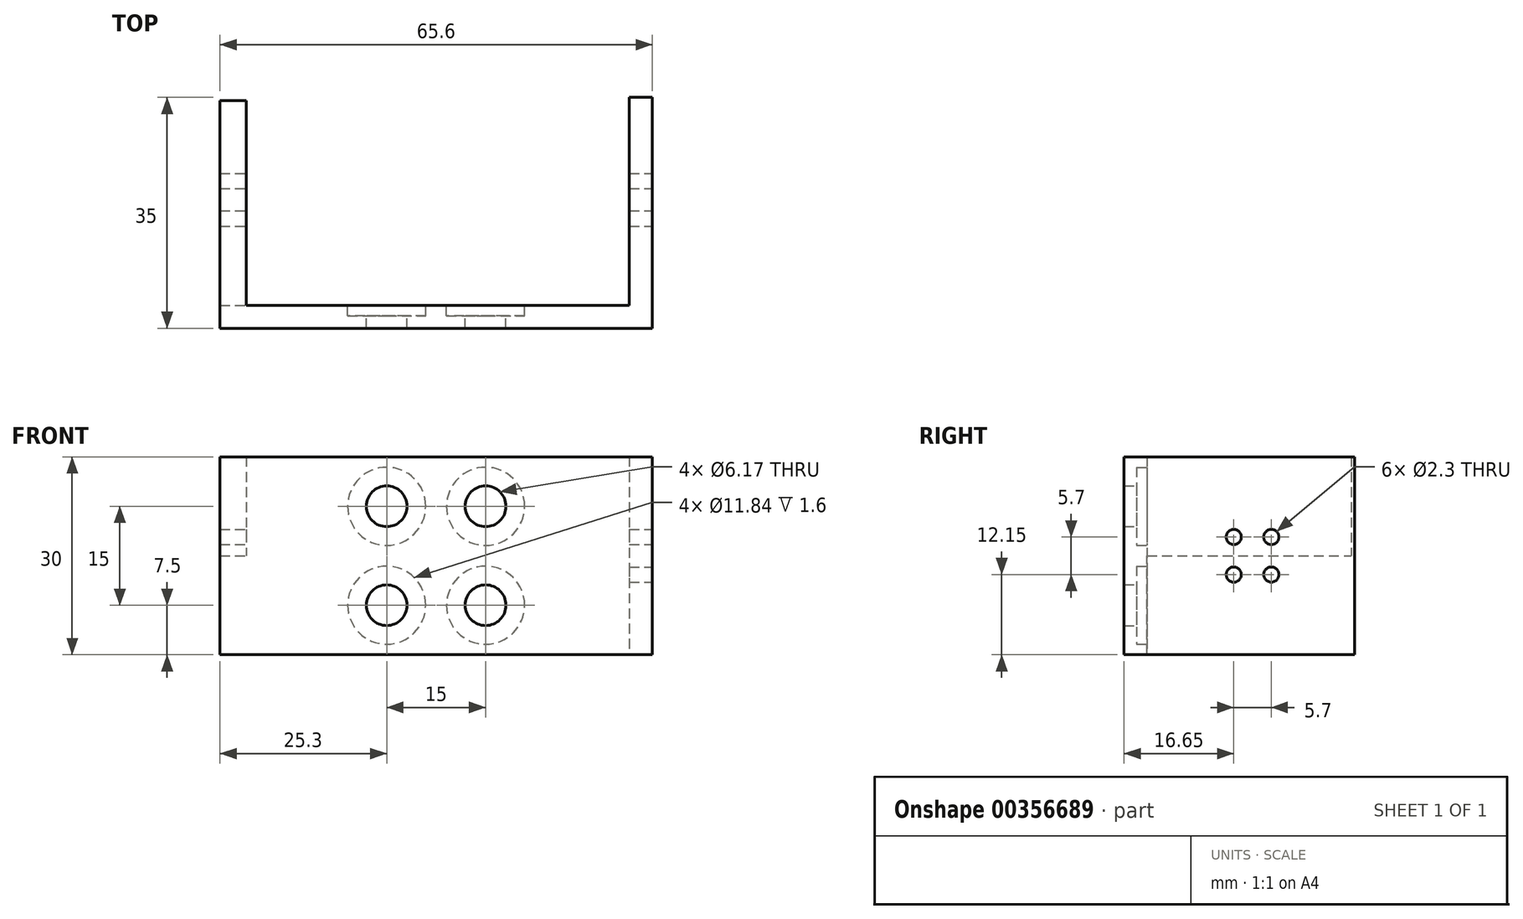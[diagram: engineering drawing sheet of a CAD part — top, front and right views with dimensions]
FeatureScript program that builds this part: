
annotation { "Feature Type Name" : "Feature", "Feature Type Description" : "" }
export const myFeature = defineFeature(function(context is Context, id is Id, definition is map)
    precondition{}
    {
        {
            var Q0;
            Q0=qCreatedBy(makeId("Front.planeOp"),FACE);
            var sketch = newSketch(context, id + "F0", { "sketchPlane" : qUnion([Q0])});
            skLineSegment(sketch, "E0.bottom", {"start": v(32.8, -15) * mm, "end": v(-32.8, -15) * mm});
            skLineSegment(sketch, "E0.top", {"start": v(32.8, 15) * mm, "end": v(-32.8, 15) * mm});
            skLineSegment(sketch, "E0.left", {"start": v(32.8, -15) * mm, "end": v(32.8, 15) * mm});
            skLineSegment(sketch, "E0.right", {"start": v(-32.8, -15) * mm, "end": v(-32.8, 15) * mm});
            skPoint(sketch, "E0.middle", {"position": v(0, 0) * mm});
            skSolve(sketch);
        }
        {
            var Q0;
            Q0=qSketchRegion(id+"F0",true);
            extrude(context, id + "F1", {"entities" : qUnion([Q0]), "endBound" : BoundingType.SYMMETRIC, "depth" : 3.5 * mm});
        }
        {
            var Q0;
            Q0=qCreatedBy(makeId("Top.planeOp"),FACE);
            var sketch = newSketch(context, id + "F2", { "sketchPlane" : qUnion([Q0])});
            skLineSegment(sketch, "E1.bottom", {"start": v(32.8, 1.75) * mm, "end": v(29.3, 1.75) * mm});
            skLineSegment(sketch, "E1.top", {"start": v(32.8, 33.25) * mm, "end": v(29.3, 33.25) * mm});
            skLineSegment(sketch, "E1.left", {"start": v(32.8, 1.75) * mm, "end": v(32.8, 33.25) * mm});
            skLineSegment(sketch, "E1.right", {"start": v(29.3, 1.75) * mm, "end": v(29.3, 33.25) * mm});
            skSolve(sketch);
        }
        {
            var Q0;
            Q0=qSketchRegion(id+"F2",true);
            extrude(context, id + "F3", {"entities" : qUnion([Q0]), "operationType" : NewBodyOperationType.ADD, "endBound" : BoundingType.SYMMETRIC, "depth" : 30 * mm});
        }
        {
            var Q0;
            Q0=qCreatedBy(makeId("Top.planeOp"),FACE);
            var sketch = newSketch(context, id + "F4", { "sketchPlane" : qUnion([Q0])});
            skLineSegment(sketch, "E2.bottom", {"start": v(-32.8, 1.75) * mm, "end": v(-28.8, 1.75) * mm});
            skLineSegment(sketch, "E2.top", {"start": v(-32.8, 32.75) * mm, "end": v(-28.8, 32.75) * mm});
            skLineSegment(sketch, "E2.left", {"start": v(-32.8, 1.75) * mm, "end": v(-32.8, 32.75) * mm});
            skLineSegment(sketch, "E2.right", {"start": v(-28.8, 1.75) * mm, "end": v(-28.8, 32.75) * mm});
            skSolve(sketch);
        }
        {
            var Q0;
            Q0=qSketchRegion(id+"F4",true);
            extrude(context, id + "F5", {"entities" : qUnion([Q0]), "operationType" : NewBodyOperationType.ADD, "depth" : 15 * mm});
        }
        {
            var Q0;
            Q0=makeQuery(id+"F3.boolean.opBoolean","MERGE",FACE,{"derivedFrom":[makeQuery(id+"F1.opExtrude","SWEPT_FACE",FACE,{"disambiguationData":[OSD([sQuery(id+"F0.wireOp",EDGE,"E0.left")])]}),makeQuery(id+"F3.opExtrude","SWEPT_FACE",FACE,{"disambiguationData":[OSD([sQuery(id+"F2.wireOp",EDGE,"E1.left")])]})]});
            var sketch = newSketch(context, id + "F6", { "sketchPlane" : qUnion([Q0])});
            skCircle(sketch, "E3", {"center": v(14.9, 2.85) * mm, "radius": 1.15 * mm});
            skCircle(sketch, "E4", {"center": v(20.6, 2.85) * mm, "radius": 1.15 * mm});
            skCircle(sketch, "E5", {"center": v(14.9, -2.85) * mm, "radius": 1.15 * mm});
            skCircle(sketch, "E6", {"center": v(20.6, -2.85) * mm, "radius": 1.15 * mm});
            skLineSegment(sketch, "E7", {"start": v(14.9, 2.85) * mm, "end": v(14.9, -2.85) * mm, "construction": true});
            skLineSegment(sketch, "E8", {"start": v(14.9, -2.85) * mm, "end": v(20.6, -2.85) * mm, "construction": true});
            skLineSegment(sketch, "E9", {"start": v(20.6, -2.85) * mm, "end": v(20.6, 2.85) * mm, "construction": true});
            skLineSegment(sketch, "E10", {"start": v(20.6, 2.85) * mm, "end": v(14.9, 2.85) * mm, "construction": true});
            skSolve(sketch);
        }
        {
            var Q0;
            Q0=qSketchRegion(id+"F6",true);
            extrude(context, id + "F7", {"entities" : qUnion([Q0]), "operationType" : NewBodyOperationType.REMOVE, "oppositeDirection" : true, "depth" : 200 * mm});
        }
        {
            var Q0;
            Q0=makeQuery(id+"F1.opExtrude","CAP_FACE",FACE,{"disambiguationData":[OSD([sQuery(id+"F0.wireOp",EDGE,"E0.bottom"),sQuery(id+"F0.wireOp",EDGE,"E0.top"),sQuery(id+"F0.wireOp",EDGE,"E0.left"),sQuery(id+"F0.wireOp",EDGE,"E0.right")])],"isStart":true});
            var sketch = newSketch(context, id + "F8", { "sketchPlane" : qUnion([Q0])});
            skCircle(sketch, "E11", {"center": v(-7.5, 7.5) * mm, "radius": 3.09 * mm});
            skCircle(sketch, "E12", {"center": v(-7.5, -7.5) * mm, "radius": 3.09 * mm});
            skCircle(sketch, "E13", {"center": v(7.5, 7.5) * mm, "radius": 3.09 * mm});
            skCircle(sketch, "E14", {"center": v(7.5, -7.5) * mm, "radius": 3.09 * mm});
            skLineSegment(sketch, "E15", {"start": v(-7.5, 7.5) * mm, "end": v(0, 7.5) * mm, "construction": true});
            skLineSegment(sketch, "E16", {"start": v(7.5, 7.5) * mm, "end": v(0, 7.5) * mm, "construction": true});
            skLineSegment(sketch, "E17", {"start": v(7.5, 7.5) * mm, "end": v(7.5, 0) * mm, "construction": true});
            skLineSegment(sketch, "E18", {"start": v(7.5, -7.5) * mm, "end": v(7.5, 0) * mm, "construction": true});
            skLineSegment(sketch, "E19", {"start": v(7.5, -7.5) * mm, "end": v(0, -7.5) * mm, "construction": true});
            skLineSegment(sketch, "E20", {"start": v(0, -7.5) * mm, "end": v(-7.5, -7.5) * mm, "construction": true});
            skLineSegment(sketch, "E21", {"start": v(-7.5, -7.5) * mm, "end": v(-7.5, 0) * mm, "construction": true});
            skLineSegment(sketch, "E22", {"start": v(-7.5, 0) * mm, "end": v(-7.5, 7.5) * mm, "construction": true});
            skSolve(sketch);
        }
        {
            var Q0;
            Q0=qSketchRegion(id+"F8",true);
            extrude(context, id + "F9", {"entities" : qUnion([Q0]), "operationType" : NewBodyOperationType.REMOVE, "oppositeDirection" : true, "depth" : 25 * mm});
        }
        {
            var Q0;
            Q0=makeQuery(id+"F1.opExtrude","CAP_FACE",FACE,{"disambiguationData":[OSD([sQuery(id+"F0.wireOp",EDGE,"E0.bottom"),sQuery(id+"F0.wireOp",EDGE,"E0.top"),sQuery(id+"F0.wireOp",EDGE,"E0.left"),sQuery(id+"F0.wireOp",EDGE,"E0.right")])],"isStart":true});
            var sketch = newSketch(context, id + "F10", { "sketchPlane" : qUnion([Q0])});
            skCircle(sketch, "E23", {"center": v(-7.5, 7.5) * mm, "radius": 5.92 * mm});
            skCircle(sketch, "E24", {"center": v(-7.5, -7.5) * mm, "radius": 5.92 * mm});
            skCircle(sketch, "E25", {"center": v(7.5, -7.5) * mm, "radius": 5.92 * mm});
            skCircle(sketch, "E26", {"center": v(7.5, 7.5) * mm, "radius": 5.92 * mm});
            skSolve(sketch);
        }
        {
            var Q0;
            Q0=qSketchRegion(id+"F10",true);
            extrude(context, id + "F11", {"entities" : qUnion([Q0]), "operationType" : NewBodyOperationType.REMOVE, "oppositeDirection" : true, "depth" : 1.6 * mm});
        }
    });
